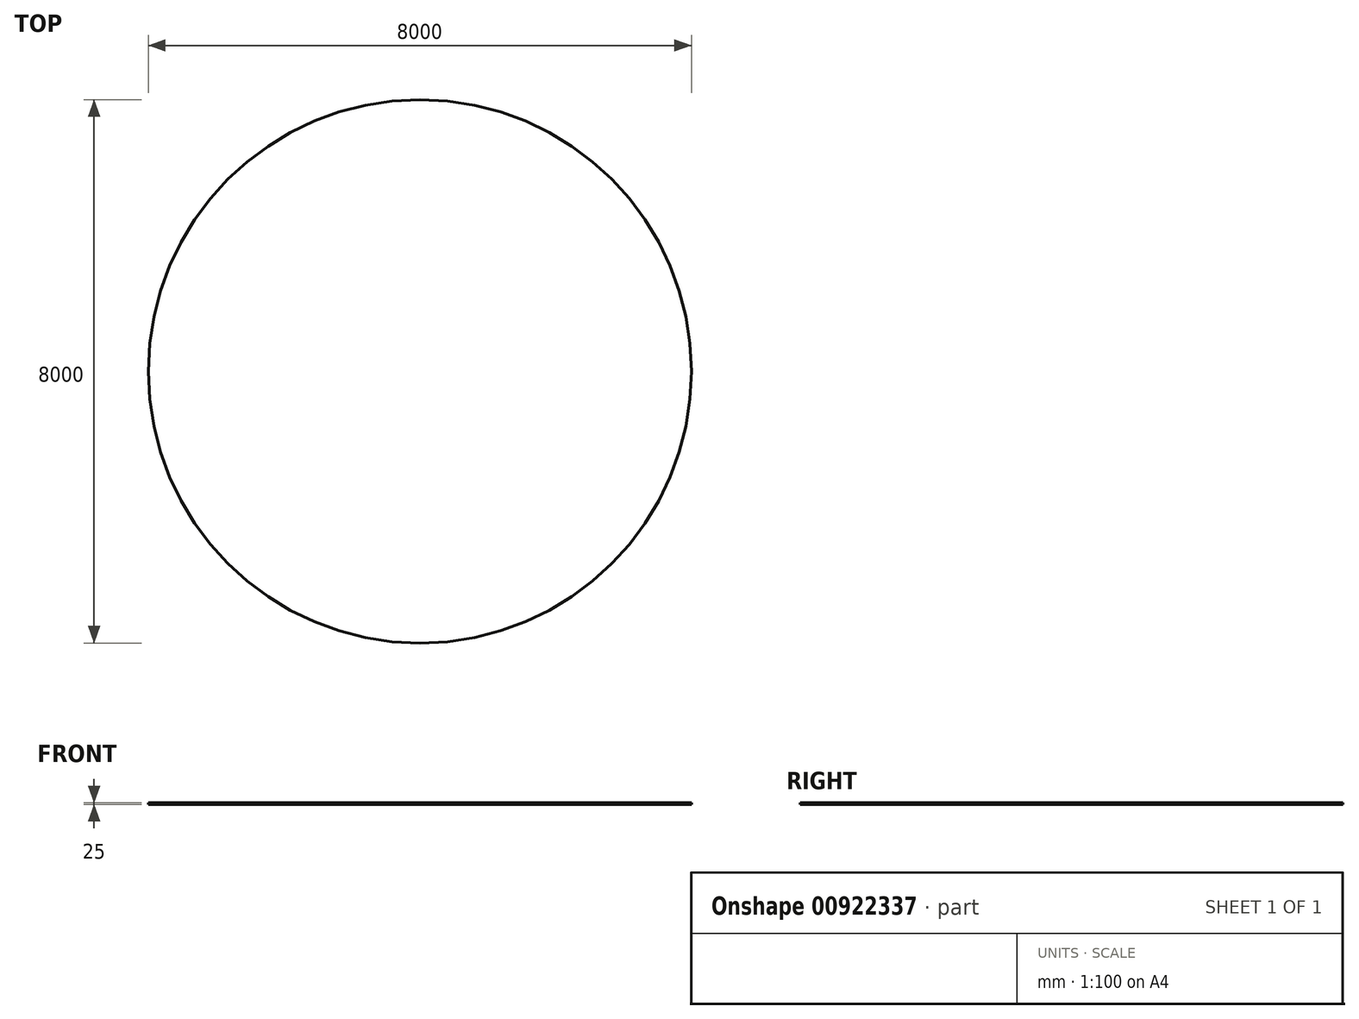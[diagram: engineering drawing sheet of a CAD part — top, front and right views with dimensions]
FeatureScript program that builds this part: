
annotation { "Feature Type Name" : "Feature", "Feature Type Description" : "" }
export const myFeature = defineFeature(function(context is Context, id is Id, definition is map)
    precondition{}
    {
        {
            var Q0;
            Q0=qCreatedBy(makeId("Top.planeOp"),FACE);
            var sketch = newSketch(context, id + "F0", { "sketchPlane" : qUnion([Q0])});
            skCircle(sketch, "E0", {"center": v(0, 0) * mm, "radius": 4000 * mm});
            skSolve(sketch);
        }
        {
            var Q0;
            Q0=makeQuery(id+"F0.imprint","IMPRINT",FACE,{"disambiguationData":[TD([[makeQuery(id+"F0.imprint","IMPRINT",EDGE,{"derivedFrom":sQuery(id+"F0.wireOp",EDGE,"E0")}),1.0]])]});
            extrude(context, id + "F1", {"entities" : qUnion([Q0]), "depth" : 25 * mm, "offsetDistance" : 25 * mm});
        }
    });
